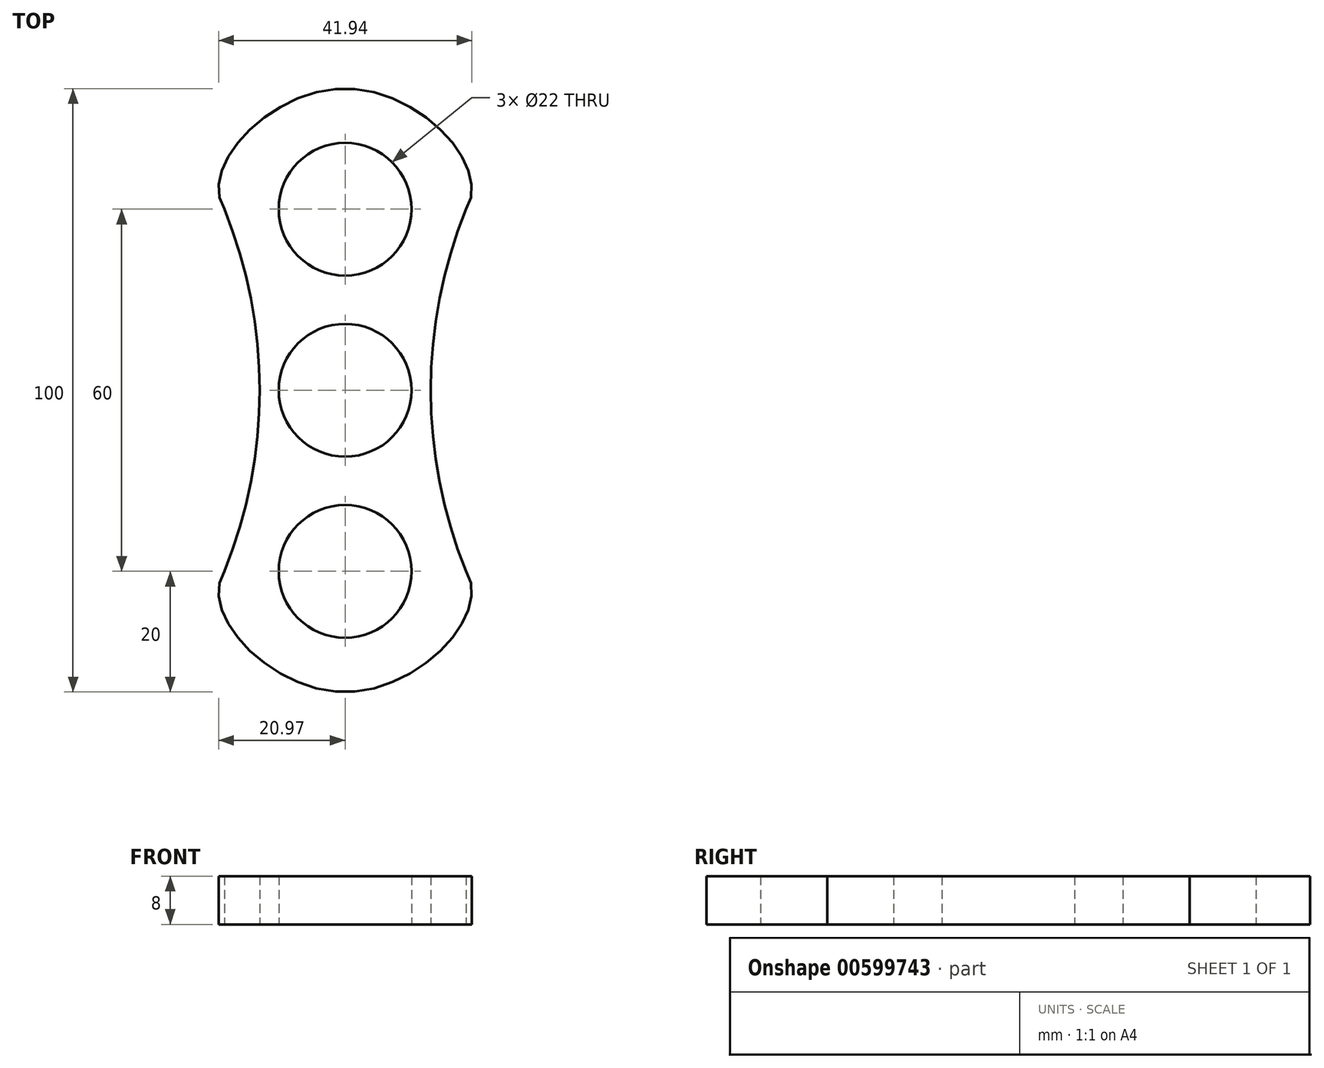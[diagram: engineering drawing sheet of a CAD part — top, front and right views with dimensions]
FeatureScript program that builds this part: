
annotation { "Feature Type Name" : "Feature", "Feature Type Description" : "" }
export const myFeature = defineFeature(function(context is Context, id is Id, definition is map)
    precondition{}
    {
        {
            var Q0;
            Q0=qCreatedBy(makeId("Top.planeOp"),FACE);
            var sketch = newSketch(context, id + "F0", { "sketchPlane" : qUnion([Q0])});
            skCircle(sketch, "E0", {"center": v(0, 0) * mm, "radius": 11 * mm});
            skCircle(sketch, "E1", {"center": v(0, 30) * mm, "radius": 11 * mm});
            skCircle(sketch, "E2", {"center": v(0, -30) * mm, "radius": 11 * mm});
            skPoint(sketch, "E3", {"position": v(0, 50) * mm});
            skPoint(sketch, "E4", {"position": v(0, -50) * mm});
            skPoint(sketch, "E5", {"position": v(20, 0) * mm});
            skPoint(sketch, "E6", {"position": v(-20, 0) * mm});
            skPoint(sketch, "E7", {"position": v(-20, 30) * mm});
            skPoint(sketch, "E8", {"position": v(20, 30) * mm});
            skPoint(sketch, "E9", {"position": v(20, -30) * mm});
            skPoint(sketch, "E10", {"position": v(-20, -30) * mm});
            skFitSpline(sketch, "E11", {"points": [v(20, 30) * mm, v(0, 50) * mm, v(-20, 30) * mm, v(20, 30) * mm]});
            skFitSpline(sketch, "E12", {"points": [v(20, -30) * mm, v(0, -50) * mm, v(-20, -30) * mm, v(20, -30) * mm]});
            skArc(sketch, "E13", {"start": v(20, 30) * mm, "mid": v(14.16, 0) * mm, "end": v(20, -30) * mm});
            skArc(sketch, "E14", {"start": v(-20, -30) * mm, "mid": v(-14.16, 0) * mm, "end": v(-20, 30) * mm});
            skSolve(sketch);
        }
        {
            var Q0;
            {var subQ0=sQuery(id+"F0.wireOp",EDGE,"E11");var subQ1=sQuery(id+"F0.wireOp",EDGE,"E1");var subQ2=makeQuery(id+"F0.imprint","INTERSECT",VERTEX,{"disambiguationData":[OD(0.0)],"derivedFrom":[subQ1,subQ0]});Q0=makeQuery(id+"F0.imprint","IMPRINT",FACE,{"disambiguationData":[TD([[makeQuery(id+"F0.imprint","IMPRINT",EDGE,{"disambiguationData":[TD([[subQ2,1.0]])],"derivedFrom":subQ1}),-1.0]])]});}
            var Q1;
            Q1=makeQuery(id+"F0.imprint","IMPRINT",FACE,{"disambiguationData":[TD([[makeQuery(id+"F0.imprint","IMPRINT",EDGE,{"derivedFrom":sQuery(id+"F0.wireOp",EDGE,"E0")}),-1.0]])]});
            var Q2;
            {var subQ0=sQuery(id+"F0.wireOp",EDGE,"E12");var subQ1=sQuery(id+"F0.wireOp",EDGE,"E2");var subQ2=makeQuery(id+"F0.imprint","INTERSECT",VERTEX,{"disambiguationData":[OD(0.0)],"derivedFrom":[subQ1,subQ0]});Q2=makeQuery(id+"F0.imprint","IMPRINT",FACE,{"disambiguationData":[TD([[makeQuery(id+"F0.imprint","IMPRINT",EDGE,{"disambiguationData":[TD([[subQ2,-1.0]])],"derivedFrom":subQ1}),-1.0]])]});}
            var Q3;
            Q3=sQuery(id+"F0.wireOp",EDGE,"E11");
            var Q4;
            Q4=sQuery(id+"F0.wireOp",EDGE,"2DePHttP-W00S-kKNN-CNeR-vN1BPuLvdWWi");
            var Q5;
            Q5=sQuery(id+"F0.wireOp",EDGE,"AGsosM8e-DtR0-SBxc-Nua2-UfuVklOzKhjo");
            var Q6;
            Q6=sQuery(id+"F0.wireOp",EDGE,"E12");
            extrude(context, id + "F1", {"entities" : qUnion([Q0, Q1, Q2]), "surfaceEntities" : qUnion([Q3, Q4, Q5, Q6]), "depth" : 8 * mm, "offsetDistance" : 25 * mm});
        }
    });
